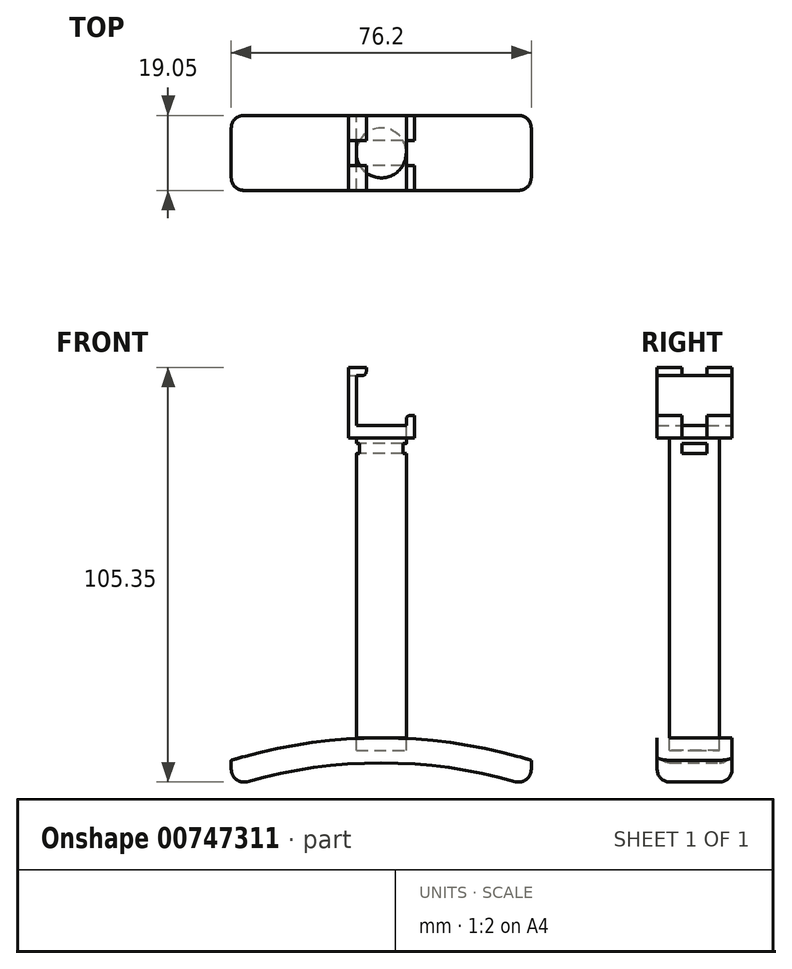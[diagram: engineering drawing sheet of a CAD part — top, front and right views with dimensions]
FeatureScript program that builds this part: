
annotation { "Feature Type Name" : "Feature", "Feature Type Description" : "" }
export const myFeature = defineFeature(function(context is Context, id is Id, definition is map)
    precondition{}
    {
        {
            var Q0;
            Q0=qCreatedBy(makeId("Front.planeOp"),FACE);
            var sketch = newSketch(context, id + "F0", { "sketchPlane" : qUnion([Q0])});
            skLineSegment(sketch, "E0.bottom", {"start": v(0, 0) * mm, "end": v(16.76, 0) * mm});
            skLineSegment(sketch, "E0.top", {"start": v(0, 17.9) * mm, "end": v(16.76, 17.9) * mm});
            skLineSegment(sketch, "E0.left", {"start": v(0, 0) * mm, "end": v(0, 17.9) * mm});
            skLineSegment(sketch, "E0.right", {"start": v(16.76, 0) * mm, "end": v(16.76, 17.9) * mm});
            skLineSegment(sketch, "E1.bottom", {"start": v(14.73, 3.18) * mm, "end": v(2.03, 3.17) * mm});
            skLineSegment(sketch, "E1.top", {"start": v(14.73, 15.88) * mm, "end": v(2.03, 15.88) * mm});
            skLineSegment(sketch, "E1.left", {"start": v(14.73, 3.17) * mm, "end": v(14.73, 15.88) * mm});
            skLineSegment(sketch, "E1.right", {"start": v(2.03, 3.17) * mm, "end": v(2.03, 15.88) * mm});
            skSolve(sketch);
        }
        {
            var Q0;
            Q0 = qSketchRegion(id + "F0", true);
            extrude(context, id + "F1", {"entities" : qUnion([Q0]), "depth" : 19.05 * mm, "offsetDistance" : 25.4 * mm});
        }
        {
            var Q0;
            Q0=qCreatedBy(makeId("Front.planeOp"),FACE);
            var sketch = newSketch(context, id + "F2", { "sketchPlane" : qUnion([Q0])});
            skLineSegment(sketch, "E2.bottom", {"start": v(4.57, 23.54) * mm, "end": v(25.76, 23.54) * mm});
            skLineSegment(sketch, "E2.top", {"start": v(4.57, 5.72) * mm, "end": v(25.76, 5.72) * mm});
            skLineSegment(sketch, "E2.left", {"start": v(4.57, 23.54) * mm, "end": v(4.57, 5.71) * mm});
            skLineSegment(sketch, "E2.right", {"start": v(25.76, 23.54) * mm, "end": v(25.76, 5.72) * mm});
            skSolve(sketch);
        }
        {
            var Q0;
            Q0 = qSketchRegion(id + "F2", true);
            extrude(context, id + "F3", {"entities" : qUnion([Q0]), "operationType" : NewBodyOperationType.REMOVE, "depth" : 25.4 * mm, "offsetDistance" : 25.4 * mm});
        }
        {
            var Q0;
            Q0=makeQuery(id+"F1.opExtrude","SWEPT_FACE",FACE,{"disambiguationData":[OSD([sQuery(id+"F0.wireOp",EDGE,"E0.bottom")])]});
            var sketch = newSketch(context, id + "F4", { "sketchPlane" : qUnion([Q0])});
            skCircle(sketch, "E3", {"center": v(8.38, 9.53) * mm, "radius": 8.38 * mm});
            skCircle(sketch, "E4", {"center": v(8.38, 9.53) * mm, "radius": 6.35 * mm});
            skSolve(sketch);
        }
        {
            var Q0;
            Q0=makeQuery(id+"F4.imprint","IMPRINT",FACE,{"disambiguationData":[TD([[makeQuery(id+"F4.imprint","IMPRINT",EDGE,{"derivedFrom":sQuery(id+"F4.wireOp",EDGE,"E4")}),1.0]])]});
            extrude(context, id + "F5", {"entities" : qUnion([Q0]), "operationType" : NewBodyOperationType.ADD, "depth" : 76.2 * mm, "offsetDistance" : 25.4 * mm});
        }
        {
            var Q0;
            Q0=qCreatedBy(makeId("Front.planeOp"),FACE);
            var sketch = newSketch(context, id + "F6", { "sketchPlane" : qUnion([Q0])});
            skArc(sketch, "E5", {"start": v(46.48, -81.9) * mm, "mid": v(8.38, -76.2) * mm, "end": v(-29.72, -81.9) * mm});
            skArc(sketch, "E6", {"start": v(46.48, -88.55) * mm, "mid": v(8.38, -82.55) * mm, "end": v(-29.72, -88.55) * mm});
            skPoint(sketch, "E7", {"position": v(8.38, -76.2) * mm});
            skLineSegment(sketch, "E8", {"start": v(-29.72, -88.55) * mm, "end": v(-29.72, -81.9) * mm});
            skLineSegment(sketch, "E9", {"start": v(46.48, -88.55) * mm, "end": v(46.48, -81.9) * mm});
            skSolve(sketch);
        }
        {
            var Q0;
            Q0 = qSketchRegion(id + "F6", true);
            extrude(context, id + "F7", {"entities" : qUnion([Q0]), "operationType" : NewBodyOperationType.ADD, "depth" : 19.05 * mm, "offsetDistance" : 25.4 * mm});
        }
        {
            var Q0;
            Q0=makeQuery(id+"F4.imprint","IMPRINT",FACE,{"disambiguationData":[TD([[makeQuery(id+"F4.imprint","IMPRINT",EDGE,{"derivedFrom":sQuery(id+"F4.wireOp",EDGE,"E4")}),1.0]])]});
            extrude(context, id + "F8", {"entities" : qUnion([Q0]), "depth" : 79.38 * mm, "offsetDistance" : 25.4 * mm});
        }
        {
            var Q0;
            Q0=makeQuery(id+"F7.opExtrude","CAP_EDGE",EDGE,{"disambiguationData":[OSD([sQuery(id+"F6.wireOp",EDGE,"E6")])],"isStart":false});
            var Q1;
            Q1=makeQuery(id+"F7.opExtrude","SWEPT_EDGE",EDGE,{"disambiguationData":[OSD([sQuery(id+"F6.wireOp",EDGE,"E6"),sQuery(id+"F6.wireOp",EDGE,"E9")])]});
            var Q2;
            Q2=makeQuery(id+"F7.opExtrude","CAP_EDGE",EDGE,{"disambiguationData":[OSD([sQuery(id+"F6.wireOp",EDGE,"E9")])],"isStart":false});
            var Q3;
            Q3=makeQuery(id+"F7.opExtrude","CAP_EDGE",EDGE,{"disambiguationData":[OSD([sQuery(id+"F6.wireOp",EDGE,"E8")])],"isStart":false});
            var Q4;
            Q4=makeQuery(id+"F7.opExtrude","CAP_EDGE",EDGE,{"disambiguationData":[OSD([sQuery(id+"F6.wireOp",EDGE,"E8")])],"isStart":true});
            var Q5;
            Q5=makeQuery(id+"F7.opExtrude","CAP_EDGE",EDGE,{"disambiguationData":[OSD([sQuery(id+"F6.wireOp",EDGE,"E6")])],"isStart":true});
            var Q6;
            Q6=makeQuery(id+"F7.opExtrude","SWEPT_EDGE",EDGE,{"disambiguationData":[OSD([sQuery(id+"F6.wireOp",EDGE,"E6"),sQuery(id+"F6.wireOp",EDGE,"E8")])]});
            var Q7;
            Q7=makeQuery(id+"F7.opExtrude","CAP_EDGE",EDGE,{"disambiguationData":[OSD([sQuery(id+"F6.wireOp",EDGE,"E9")])],"isStart":true});
            fillet(context, id + "F9", {"entities" : qUnion([Q0, Q1, Q2, Q3, Q4, Q5, Q6, Q7]), "radius" : 3.17 * mm, "tangentPropagation" : true, "allowEdgeOverflow" : false});
        }
        {
            var Q0;
            Q0=makeQuery(id+"F3.boolean.opBoolean","INTERSECT",EDGE,{"derivedFrom":[makeQuery(id+"F1.opExtrude","SWEPT_FACE",FACE,{"disambiguationData":[OSD([sQuery(id+"F0.wireOp",EDGE,"E1.top")])]}),makeQuery(id+"F3.opExtrude","SWEPT_FACE",FACE,{"disambiguationData":[OSD([sQuery(id+"F2.wireOp",EDGE,"E2.left")])]})]});
            var Q1;
            Q1=makeQuery(id+"F3.boolean.opBoolean","INTERSECT",EDGE,{"derivedFrom":[makeQuery(id+"F1.opExtrude","SWEPT_FACE",FACE,{"disambiguationData":[OSD([sQuery(id+"F0.wireOp",EDGE,"E1.left")])]}),makeQuery(id+"F3.opExtrude","SWEPT_FACE",FACE,{"disambiguationData":[OSD([sQuery(id+"F2.wireOp",EDGE,"E2.top")])]})]});
            fillet(context, id + "F10", {"entities" : qUnion([Q0, Q1]), "radius" : 1.02 * mm, "tangentPropagation" : true, "allowEdgeOverflow" : false});
        }
        {
            var Q0;
            Q0=qCreatedBy(makeId("Right.planeOp"),FACE);
            var sketch = newSketch(context, id + "F11", { "sketchPlane" : qUnion([Q0])});
            skLineSegment(sketch, "E10.bottom", {"start": v(-12.7, -1.44) * mm, "end": v(-6.35, -1.44) * mm});
            skLineSegment(sketch, "E10.top", {"start": v(-12.7, -3.98) * mm, "end": v(-6.35, -3.98) * mm});
            skLineSegment(sketch, "E10.left", {"start": v(-12.7, -1.44) * mm, "end": v(-12.7, -3.98) * mm});
            skLineSegment(sketch, "E10.right", {"start": v(-6.35, -1.44) * mm, "end": v(-6.35, -3.98) * mm});
            skLineSegment(sketch, "E11", {"start": v(-9.53, -1.44) * mm, "end": v(-9.53, 0) * mm});
            skSolve(sketch);
        }
        {
            var Q0;
            Q0 = qSketchRegion(id + "F11", true);
            extrude(context, id + "F12", {"entities" : qUnion([Q0]), "operationType" : NewBodyOperationType.REMOVE, "depth" : 25.4 * mm, "offsetDistance" : 25.4 * mm});
        }
        {
            var Q0;
            Q0=makeQuery(id+"F12.boolean.opBoolean","COPY",FACE,{"derivedFrom":makeQuery(id+"F12.opExtrude","SWEPT_FACE",FACE,{"disambiguationData":[OSD([sQuery(id+"F11.wireOp",EDGE,"E10.right")])]})});
            var sketch = newSketch(context, id + "F13", { "sketchPlane" : qUnion([Q0])});
            skLineSegment(sketch, "E12.bottom", {"start": v(-0.93, 20.34) * mm, "end": v(8.24, 20.34) * mm});
            skLineSegment(sketch, "E12.top", {"start": v(-0.93, 15.88) * mm, "end": v(8.24, 15.88) * mm});
            skLineSegment(sketch, "E12.left", {"start": v(-0.93, 20.34) * mm, "end": v(-0.93, 15.88) * mm});
            skLineSegment(sketch, "E12.right", {"start": v(8.24, 20.34) * mm, "end": v(8.24, 15.88) * mm});
            skLineSegment(sketch, "E13.bottom", {"start": v(14.73, 7.03) * mm, "end": v(17.85, 7.03) * mm});
            skLineSegment(sketch, "E13.top", {"start": v(14.73, -1.6) * mm, "end": v(17.85, -1.6) * mm});
            skLineSegment(sketch, "E13.left", {"start": v(14.73, 7.03) * mm, "end": v(14.73, -1.6) * mm});
            skLineSegment(sketch, "E13.right", {"start": v(17.85, 7.03) * mm, "end": v(17.85, -1.6) * mm});
            skSolve(sketch);
        }
        {
            var Q0;
            Q0 = qSketchRegion(id + "F13", true);
            var Q1;
            Q1=makeQuery(id+"F12.boolean.opBoolean","COPY",FACE,{"derivedFrom":makeQuery(id+"F12.opExtrude","SWEPT_FACE",FACE,{"disambiguationData":[OSD([sQuery(id+"F11.wireOp",EDGE,"E10.left")])]})});
            extrude(context, id + "F14", {"entities" : qUnion([Q0]), "operationType" : NewBodyOperationType.REMOVE, "endBound" : BoundingType.UP_TO_SURFACE, "depth" : 25.4 * mm, "endBoundEntityFace" : qUnion([Q1]), "offsetDistance" : 25.4 * mm});
        }
    });
